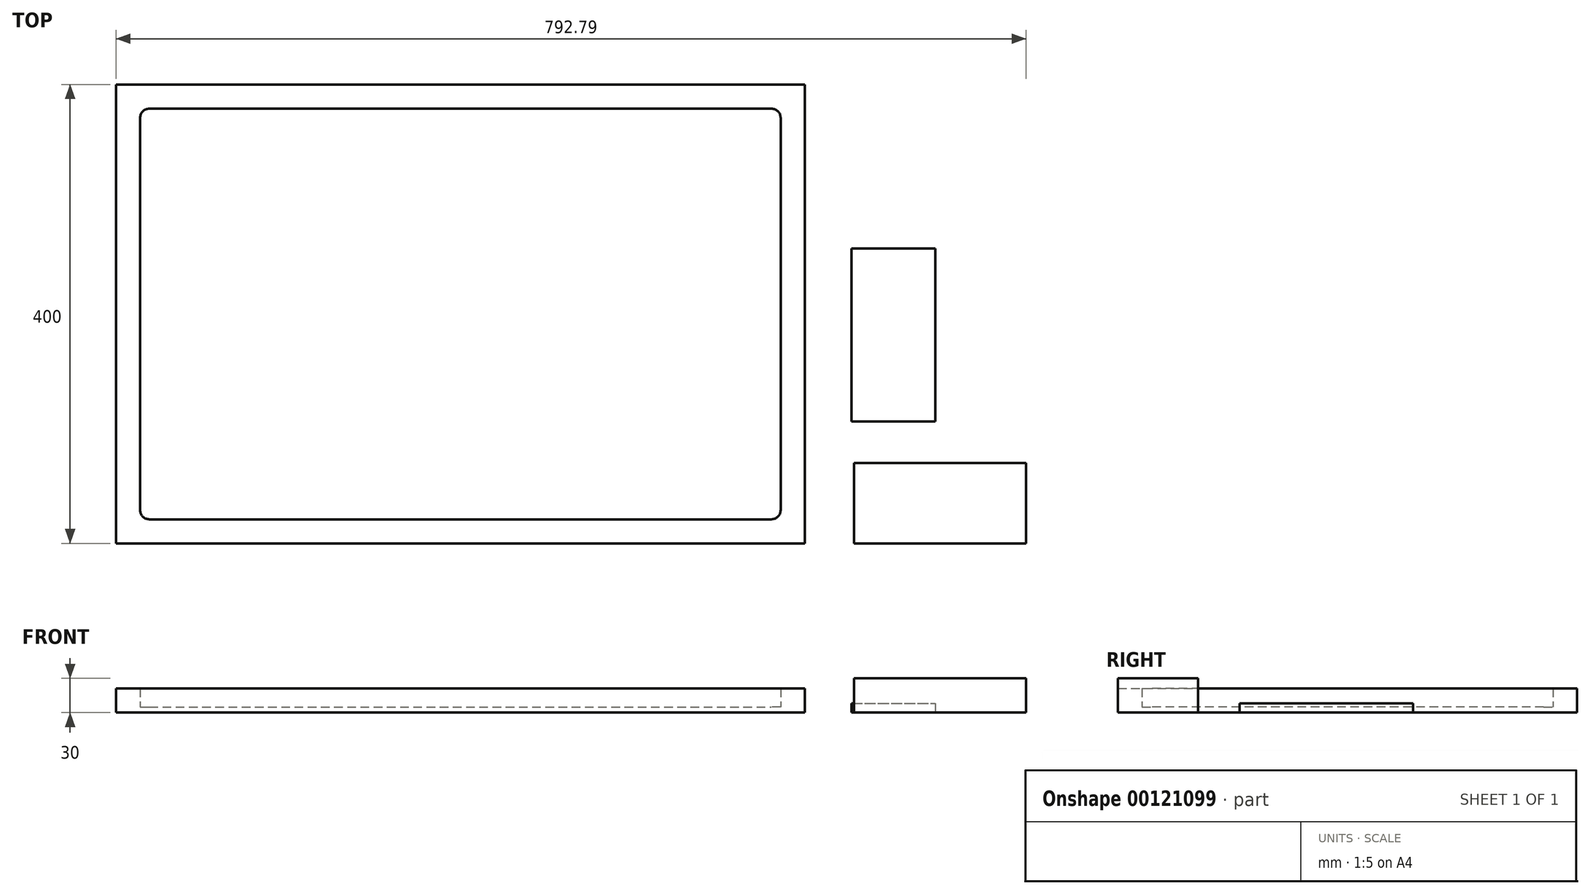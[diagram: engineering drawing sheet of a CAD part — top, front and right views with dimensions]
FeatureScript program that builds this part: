
annotation { "Feature Type Name" : "Feature", "Feature Type Description" : "" }
export const myFeature = defineFeature(function(context is Context, id is Id, definition is map)
    precondition{}
    {
        {
            assignVariable(context, id + "F0", {"name" : "d", "anyValue" : 21});
        }
        {
            var Q0;
            Q0=qCreatedBy(makeId("Top.planeOp"),FACE);
            var sketch = newSketch(context, id + "F1", { "sketchPlane" : qUnion([Q0])});
            skLineSegment(sketch, "E0.bottom", {"start": v(0, 0) * mm, "end": v(600, 0) * mm});
            skLineSegment(sketch, "E0.top", {"start": v(0, 400) * mm, "end": v(600, 400) * mm});
            skLineSegment(sketch, "E0.left", {"start": v(0, 0) * mm, "end": v(0, 400) * mm});
            skLineSegment(sketch, "E0.right", {"start": v(600, 0) * mm, "end": v(600, 400) * mm});
            skLineSegment(sketch, "E1.bottom", {"start": v(29, 379) * mm, "end": v(571, 379) * mm});
            skLineSegment(sketch, "E1.top", {"start": v(29, 21) * mm, "end": v(571, 21) * mm});
            skLineSegment(sketch, "E1.left", {"start": v(21, 371) * mm, "end": v(21, 29) * mm});
            skLineSegment(sketch, "E1.right", {"start": v(579, 371) * mm, "end": v(579, 29) * mm});
            skPoint(sketch, "E2.visualSharp", {"position": v(21, 379) * mm});
            skArc(sketch, "E2.filletArc", {"start": v(29, 379) * mm, "mid": v(23.34, 376.66) * mm, "end": v(21, 371) * mm});
            skPoint(sketch, "E3.visualSharp", {"position": v(579, 379) * mm});
            skArc(sketch, "E3.filletArc", {"start": v(579, 371) * mm, "mid": v(576.66, 376.66) * mm, "end": v(571, 379) * mm});
            skPoint(sketch, "E4.visualSharp", {"position": v(579, 21) * mm});
            skArc(sketch, "E4.filletArc", {"start": v(571, 21) * mm, "mid": v(576.66, 23.34) * mm, "end": v(579, 29) * mm});
            skPoint(sketch, "E5.visualSharp", {"position": v(21, 21) * mm});
            skArc(sketch, "E5.filletArc", {"start": v(21, 29) * mm, "mid": v(23.34, 23.34) * mm, "end": v(29, 21) * mm});
            skLineSegment(sketch, "E6.bottom", {"start": v(642.79, 70) * mm, "end": v(792.79, 70) * mm});
            skLineSegment(sketch, "E6.top", {"start": v(642.79, 0) * mm, "end": v(792.79, 0) * mm});
            skLineSegment(sketch, "E6.left", {"start": v(642.79, 70) * mm, "end": v(642.79, 0) * mm});
            skLineSegment(sketch, "E6.right", {"start": v(792.79, 70) * mm, "end": v(792.79, 0) * mm});
            skLineSegment(sketch, "E7.bottom", {"start": v(640.67, 257.14) * mm, "end": v(713.67, 257.14) * mm});
            skLineSegment(sketch, "E7.top", {"start": v(640.67, 106.14) * mm, "end": v(713.67, 106.14) * mm});
            skLineSegment(sketch, "E7.left", {"start": v(640.67, 257.14) * mm, "end": v(640.67, 106.14) * mm});
            skLineSegment(sketch, "E7.right", {"start": v(713.67, 257.14) * mm, "end": v(713.67, 106.14) * mm});
            skSolve(sketch);
        }
        {
            var Q0;
            Q0=makeQuery(id+"F1.imprint","IMPRINT",FACE,{"disambiguationData":[TD([[makeQuery(id+"F1.imprint","IMPRINT",EDGE,{"derivedFrom":sQuery(id+"F1.wireOp",EDGE,"E0.bottom")}),1.0]])]});
            extrude(context, id + "F2", {"entities" : qUnion([Q0]), "depth" : (getVariable(context, 'd')) * mm});
        }
        {
            var Q0;
            Q0=makeQuery(id+"F1.imprint","IMPRINT",FACE,{"disambiguationData":[TD([[makeQuery(id+"F1.imprint","IMPRINT",EDGE,{"derivedFrom":sQuery(id+"F1.wireOp",EDGE,"E1.bottom")}),-1.0]])]});
            extrude(context, id + "F3", {"entities" : qUnion([Q0]), "operationType" : NewBodyOperationType.ADD, "depth" : 5 * mm});
        }
        {
            var Q0;
            Q0=makeQuery(id+"F1.imprint","IMPRINT",FACE,{"disambiguationData":[TD([[makeQuery(id+"F1.imprint","IMPRINT",EDGE,{"derivedFrom":sQuery(id+"F1.wireOp",EDGE,"E6.bottom")}),-1.0]])]});
            extrude(context, id + "F4", {"entities" : qUnion([Q0]), "depth" : 30 * mm});
        }
        {
            var Q0;
            Q0=makeQuery(id+"F1.imprint","IMPRINT",FACE,{"disambiguationData":[TD([[makeQuery(id+"F1.imprint","IMPRINT",EDGE,{"derivedFrom":sQuery(id+"F1.wireOp",EDGE,"E7.bottom")}),-1.0]])]});
            extrude(context, id + "F5", {"entities" : qUnion([Q0]), "depth" : 8 * mm});
        }
    });
